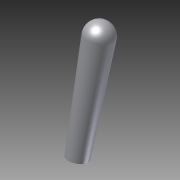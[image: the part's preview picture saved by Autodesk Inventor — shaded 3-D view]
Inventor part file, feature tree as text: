
AUTODESK INVENTOR PART (.ipt)
format: ipt  version: 2011 SP1 (Build 150282100, 282)  size: 106,496 bytes
history: native  units: in
note: dims shown in document units (in); Inventor stores cm internally (conversion verified against a paired STEP export)
features: other x28, revolve x1, sketch x1
ambient origin geometry x8: Origin, YZ Plane, XZ Plane, XY Plane, X Axis, Y Axis, Z Axis, Center Point
bodies: Solid1 (feature_tree)
feature tree (30):
  revolve  "Revolution1"  [1 undecoded]
  other  "1_righta_vertical_XY"
  other  "1_righta_vertical_YZ"
  other  "1_righta_vertical_ZX"
  other  "1_righta_vertical_X"
  other  "1_righta_vertical_Y"
  other  "1_righta_vertical_Z"
  other  "1_righta_vertical_Center"
  other  "1_straight_XY"
  other  "1_straight_YZ"
  other  "1_straight_ZX"
  other  "1_straight_X"
  other  "1_straight_Y"
  other  "1_straight_Z"
  other  "1_straight_Center"
  other  "right_vertical_l_XY"
  other  "right_vertical_l_YZ"
  other  "right_vertical_l_ZX"
  other  "right_vertical_l_X"
  other  "right_vertical_l_Y"
  other  "right_vertical_l_Z"
  other  "right_vertical_l_Center"
  other  "straight_l_XY"
  other  "straight_l_YZ"
  other  "straight_l_ZX"
  other  "straight_l_X"
  other  "straight_l_Y"
  other  "straight_l_Z"
  other  "straight_l_Center"
  sketch  "Sketch_1"  dims[d0=360.0deg]
note: 1 required parameter value undecoded (feature->parameter linkage not recoverable at this tier; creation-order binding heuristic only, values carry confidence <= 0.55)
